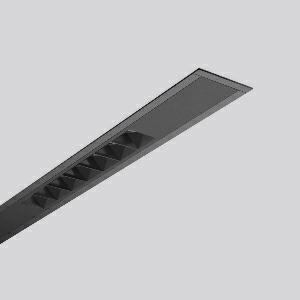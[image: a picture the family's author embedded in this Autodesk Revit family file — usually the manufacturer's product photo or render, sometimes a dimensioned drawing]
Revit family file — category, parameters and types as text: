
# Revit family: less_is_more_beamline_312470_003_e33e
name_source: partatom
category: Lighting Fixtures
units: mm (PartAtom-declared; Revit-internal decimal feet)

## family parameters
Cut with Voids When Loaded = No
Host = Face
Light Source = No
Part Type = Normal
Room Calculation Point = No
Round Connector Dimension = Use Diameter
Shared = No

## types (1)
- LESS IS MORE BEAMLINE (1 x LED Modul 930, 1825 lm, 3000)
    Apparent Load = 48 VA
    CIE Flux Codes = 100 100 100 100 100
    Color Rendering = 90
    Color Temperature = 3000
    Default Elevation = 1800 mm
    Description = Series: LESS IS MORE BEAMLINE
Linear recessed ceiling and wall luminaire for aesthetically sophisticated lighting. Luminaire with two LED light units. Housing: extruded aluminium profile, powder-coated. End cap aluminium powder-coated. LED light unit with MRS technology: Mini-Reflector-System made of metallised thermoplastic with prismatic black glare-suppressing frame for pleasant glare-free light (RUG < 10). Each LED light unit has 7 reflector elements. Wide beam light distribution. Ceiling installation with pre-assembled SBS mounting system. LED unit with integrated converter interchangeable and removable. Suitable for through-wiring. 
Colour: deep black, matt (RAL 9005)
Length: 1141 mm
Width: 71 mm
Height: 1.5 mm
Cut-out length: 1128 mm
Cut-out width: 60 mm
Recess height: 125 mm
Luminaire: recess height: 106 mm
Lamp: LED
Socket: without socket
Colour temperature: 3000K
Colour rendering index (CRI): 90
System power: 48 W
Rated luminous flux: 3650 lm
Luminous efficiency: 76 lm/W
Control gear: Regulated power supply
Protection class: I
Type of protection: IP 20
    Height = 0 mm  [stored 0 ft]
    Lamp = 1 x LED Modul 930
    Lamp Light Flux = 1825 lm
    Lamp count = 1
    Length = 1141 mm
    Lifetime = 50000 h
    Luminous efficacy = 76 lm/W
    Manufacturer = RZB
    ModVariant = No
    Model = 312470.003
    Mounting Place = Ceiling, Wall
    Mounting Type = Recessed
    Number of Poles = 1
    OnlyDefault = Yes
    Power Factor = 1
    Product Name = LESS IS MORE BEAMLINE
    Product group = Recessed LED linear luminaires
    ProductGroupID = 407
    Protection Class = Protection class I
    Protection Degree = IP 20
    RLX_Detail_Level = 1
    RLX_Emergency_Light_Flux = 0 lm
    RLX_Emergency_Type = 0
    RLX_Emergency_Type_DB = No
    RlxData = <blob elided: 23889 chars, md5=e07c5100>
    Socket = socket
    Standby Power = 0 W
    System Light Flux = 3650 lm
    System Power = 48 W
    Type Comments = Product without accessories
    Type Image = 312465.003.jpg
    URL = http://relux.com
    VarID = ---
    Voltage = 230 V
    Voltage Range = 220-240 V
    Weight = 0.00 kg
    Width = 71 mm

note: [stored X ft] marks values corroborated as IEEE doubles in the binary element streams (Revit-internal decimal feet)

## geometry (parser evidence)
native form markers: Blend x4, Sweep x13
no freeform markers — native parametric forms only
